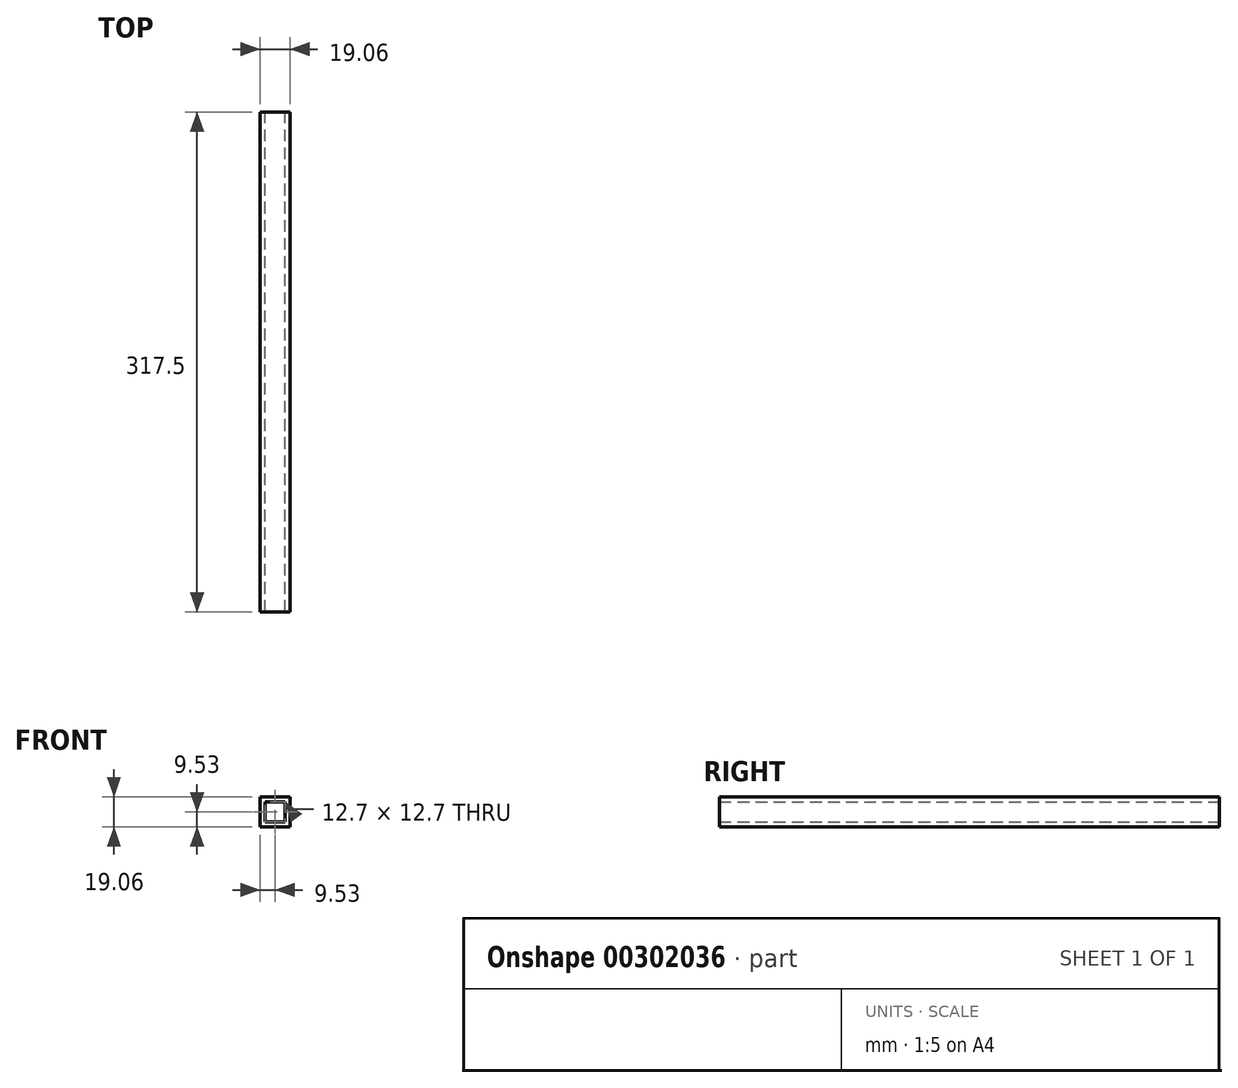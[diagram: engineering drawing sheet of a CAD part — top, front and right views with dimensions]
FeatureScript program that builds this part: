
annotation { "Feature Type Name" : "Feature", "Feature Type Description" : "" }
export const myFeature = defineFeature(function(context is Context, id is Id, definition is map)
    precondition{}
    {
        {
            var Q0;
            Q0=qCreatedBy(makeId("Front.planeOp"),FACE);
            var sketch = newSketch(context, id + "F0", { "sketchPlane" : qUnion([Q0])});
            skLineSegment(sketch, "E0.bottom", {"start": v(9.53, 9.53) * mm, "end": v(-9.53, 9.53) * mm});
            skLineSegment(sketch, "E0.top", {"start": v(9.53, -9.53) * mm, "end": v(-9.53, -9.53) * mm});
            skLineSegment(sketch, "E0.left", {"start": v(9.53, 9.53) * mm, "end": v(9.53, -9.53) * mm});
            skLineSegment(sketch, "E0.right", {"start": v(-9.53, 9.53) * mm, "end": v(-9.53, -9.53) * mm});
            skPoint(sketch, "E0.middle", {"position": v(0, 0) * mm});
            skLineSegment(sketch, "E1.bottom", {"start": v(6.35, 6.35) * mm, "end": v(-6.35, 6.35) * mm});
            skLineSegment(sketch, "E1.top", {"start": v(6.35, -6.35) * mm, "end": v(-6.35, -6.35) * mm});
            skLineSegment(sketch, "E1.left", {"start": v(6.35, 6.35) * mm, "end": v(6.35, -6.35) * mm});
            skLineSegment(sketch, "E1.right", {"start": v(-6.35, 6.35) * mm, "end": v(-6.35, -6.35) * mm});
            skSolve(sketch);
        }
        {
            var Q0;
            Q0 = qSketchRegion(id + "F0", true);
            extrude(context, id + "F1", {"entities" : qUnion([Q0]), "depth" : 317.5 * mm});
        }
    });
